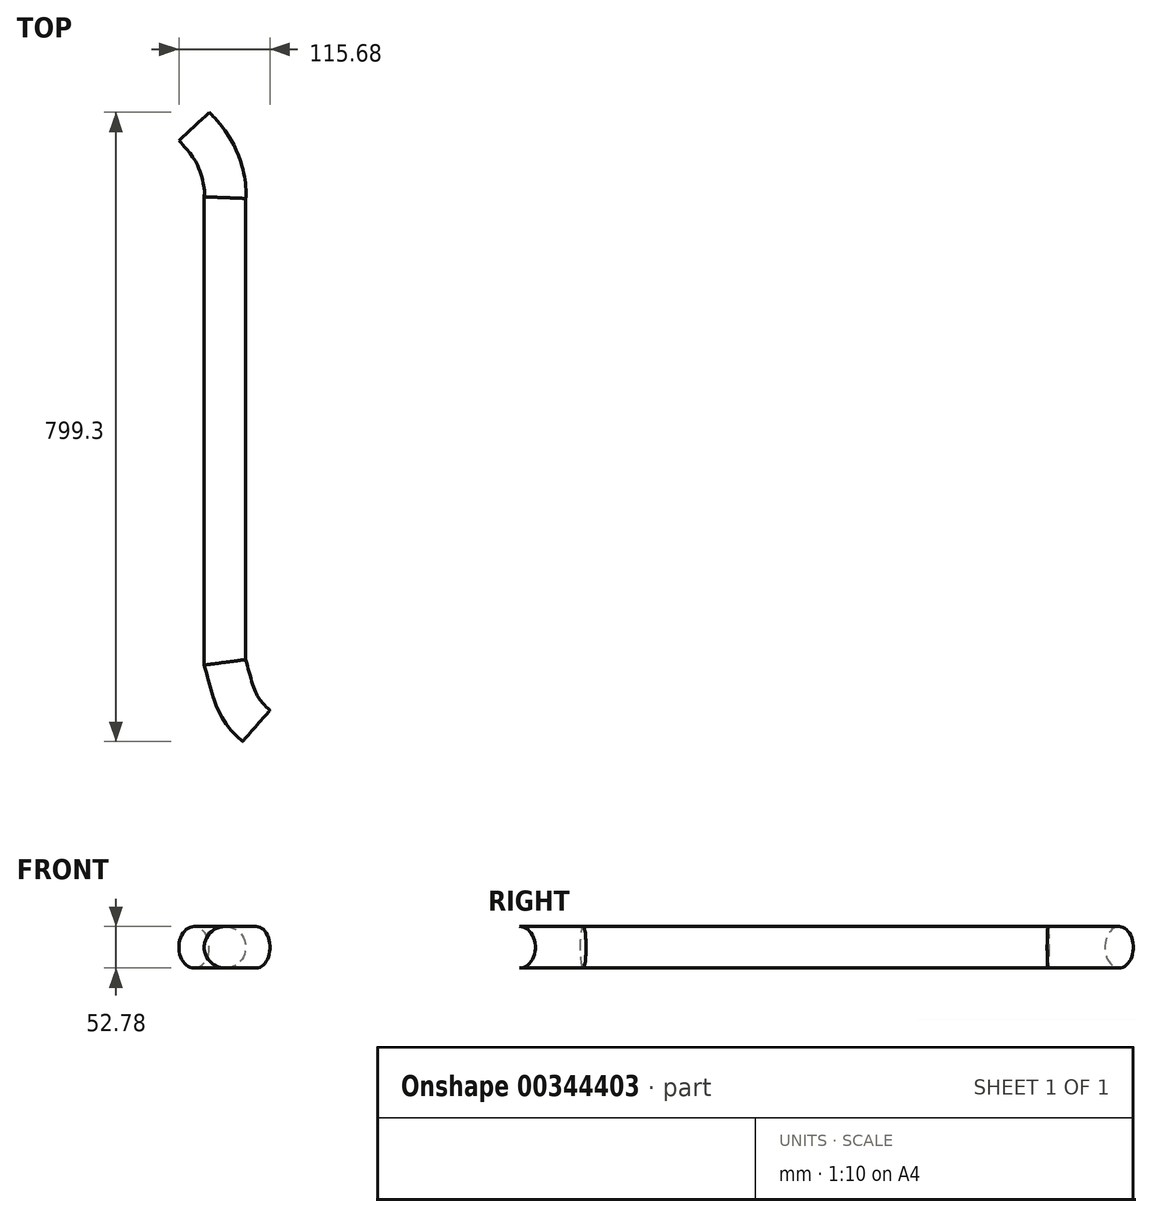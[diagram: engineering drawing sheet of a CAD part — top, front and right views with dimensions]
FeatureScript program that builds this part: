
annotation { "Feature Type Name" : "Feature", "Feature Type Description" : "" }
export const myFeature = defineFeature(function(context is Context, id is Id, definition is map)
    precondition{}
    {
        {
            var Q0;
            Q0=qCreatedBy(makeId("Front.planeOp"),FACE);
            var sketch = newSketch(context, id + "F0", { "sketchPlane" : qUnion([Q0])});
            skCircle(sketch, "E0", {"center": v(0, 0) * mm, "radius": 26.39 * mm});
            skSolve(sketch);
        }
        {
            var Q0;
            Q0=qCreatedBy(makeId("Top.planeOp"),FACE);
            var sketch = newSketch(context, id + "F1", { "sketchPlane" : qUnion([Q0])});
            skLineSegment(sketch, "E1", {"start": v(0, 0) * mm, "end": v(0, 77.16) * mm});
            skFitSpline(sketch, "E2", {"points": [v(0, 77.16) * mm, v(0, 90.48) * mm, v(-12.12, 131.87) * mm, v(-39.23, 167.55) * mm], "startDerivative": vector(4.26, 52.23) * mm, "endDerivative": vector(-75.98, 81.67) * mm});
            skSolve(sketch);
        }
        {
            var Q0;
            Q0=makeQuery(id+"F0.imprint","IMPRINT",FACE,{"disambiguationData":[TD([[makeQuery(id+"F0.imprint","IMPRINT",EDGE,{"derivedFrom":sQuery(id+"F0.wireOp",EDGE,"E0")}),1.0]])]});
            var Q1;
            Q1=sQuery(id+"F1.wireOp",EDGE,"E2");
            var Q2;
            Q2=sQuery(id+"F1.wireOp",EDGE,"E1");
            sweep(context, id + "F2", {"profiles" : qUnion([Q0]), "path" : qUnion([Q1, Q2])});
        }
        {
            var Q0;
            Q0=qCreatedBy(makeId("Top.planeOp"),FACE);
            var sketch = newSketch(context, id + "F3", { "sketchPlane" : qUnion([Q0])});
            skLineSegment(sketch, "E3", {"start": v(0, 0) * mm, "end": v(0, -513.14) * mm});
            skFitSpline(sketch, "E4", {"points": [v(0, -513.14) * mm, v(16, -564.39) * mm, v(39.8, -593.88) * mm], "startDerivative": vector(26.92, -99.6) * mm, "endDerivative": vector(77.06, -67.16) * mm});
            skSolve(sketch);
        }
        {
            var Q0;
            Q0=makeQuery(id+"F2.opSweep","CAP_FACE",FACE,{"disambiguationData":[OSD([sQuery(id+"F0.wireOp",EDGE,"E0"),sQuery(id+"F1.wireOp",VERTEX,"E1.start")])],"isStart":true});
            var Q1;
            Q1=sQuery(id+"F3.wireOp",EDGE,"E3");
            var Q2;
            Q2=sQuery(id+"F3.wireOp",EDGE,"E4");
            sweep(context, id + "F4", {"operationType" : NewBodyOperationType.ADD, "profiles" : qUnion([Q0]), "path" : qUnion([Q1, Q2])});
        }
    });
